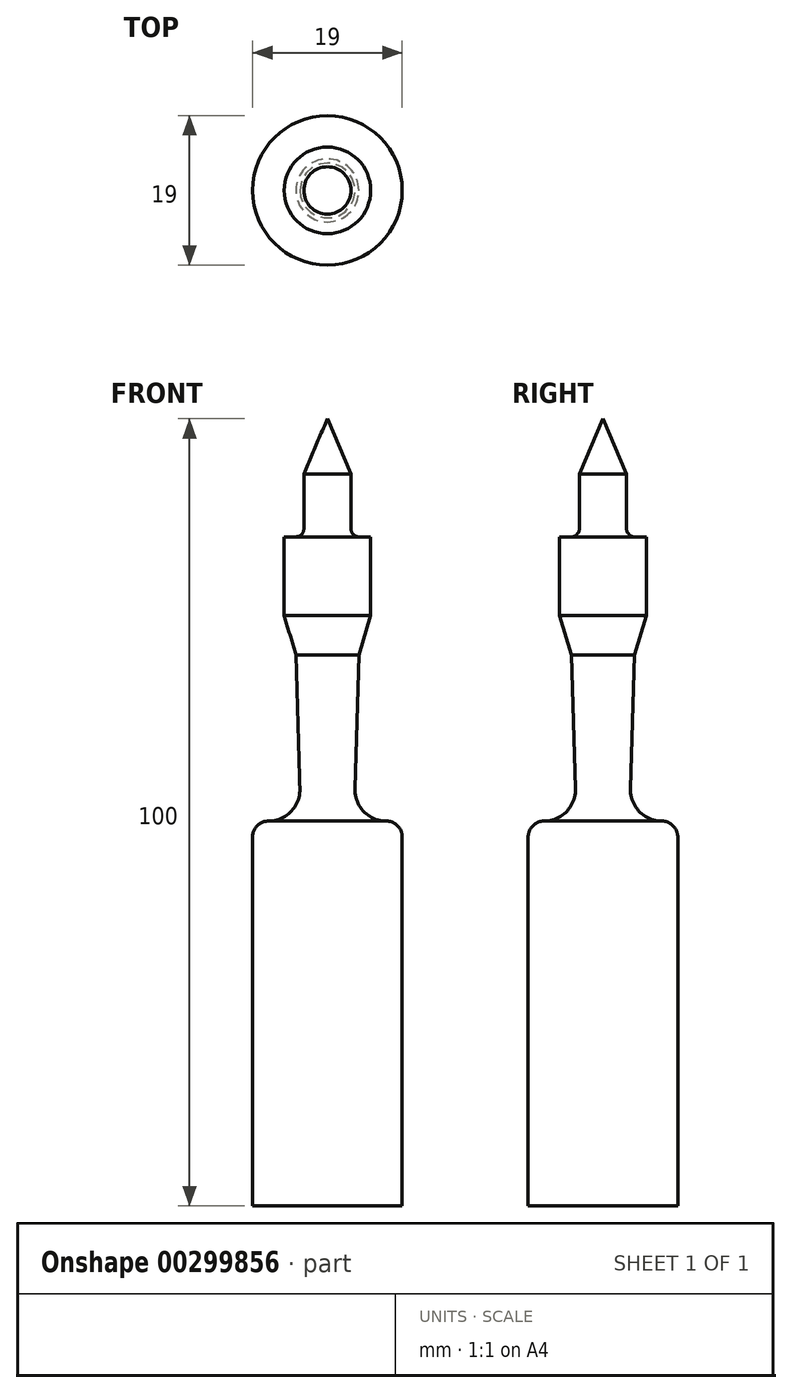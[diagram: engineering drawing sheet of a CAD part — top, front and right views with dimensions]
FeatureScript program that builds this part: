
annotation { "Feature Type Name" : "Feature", "Feature Type Description" : "" }
export const myFeature = defineFeature(function(context is Context, id is Id, definition is map)
    precondition{}
    {
        {
            var Q0;
            Q0=qCreatedBy(makeId("Front.planeOp"),FACE);
            var sketch = newSketch(context, id + "F0", { "sketchPlane" : qUnion([Q0])});
            skLineSegment(sketch, "E0", {"start": v(0, 0) * mm, "end": v(3, -7) * mm});
            skLineSegment(sketch, "E1", {"start": v(3, -7) * mm, "end": v(3, -14) * mm});
            skArc(sketch, "E2", {"start": v(3, -14) * mm, "mid": v(3.3, -14.7) * mm, "end": v(4, -15) * mm});
            skLineSegment(sketch, "E3", {"start": v(4, -15) * mm, "end": v(5.5, -15) * mm});
            skLineSegment(sketch, "E4", {"start": v(5.5, -15) * mm, "end": v(5.5, -25) * mm});
            skLineSegment(sketch, "E5", {"start": v(5.5, -25) * mm, "end": v(4, -30) * mm});
            skLineSegment(sketch, "E6", {"start": v(4, -30) * mm, "end": v(3.5, -47) * mm});
            skArc(sketch, "E7", {"start": v(3.5, -47) * mm, "mid": v(4.63, -49.9) * mm, "end": v(7.5, -51.12) * mm});
            skArc(sketch, "E8", {"start": v(9.5, -53.12) * mm, "mid": v(8.91, -51.7) * mm, "end": v(7.5, -51.12) * mm});
            skLineSegment(sketch, "E9", {"start": v(9.5, -53.12) * mm, "end": v(9.5, -100) * mm});
            skLineSegment(sketch, "E10", {"start": v(9.5, -100) * mm, "end": v(0, -100) * mm});
            skLineSegment(sketch, "E11", {"start": v(0, -100) * mm, "end": v(0, 0) * mm});
            skSolve(sketch);
        }
        {
            var Q0;
            Q0=makeQuery(id+"F0.imprint","IMPRINT",FACE,{"disambiguationData":[TD([[makeQuery(id+"F0.imprint","IMPRINT",EDGE,{"derivedFrom":sQuery(id+"F0.wireOp",EDGE,"E0")}),-1.0]])]});
            var Q1;
            Q1=sQuery(id+"F0.wireOp",EDGE,"E11");
            revolve(context, id + "F1", {"entities" : qUnion([Q0]), "axis" : qUnion([Q1]), "revolveType" : RevolveType.FULL});
        }
    });
